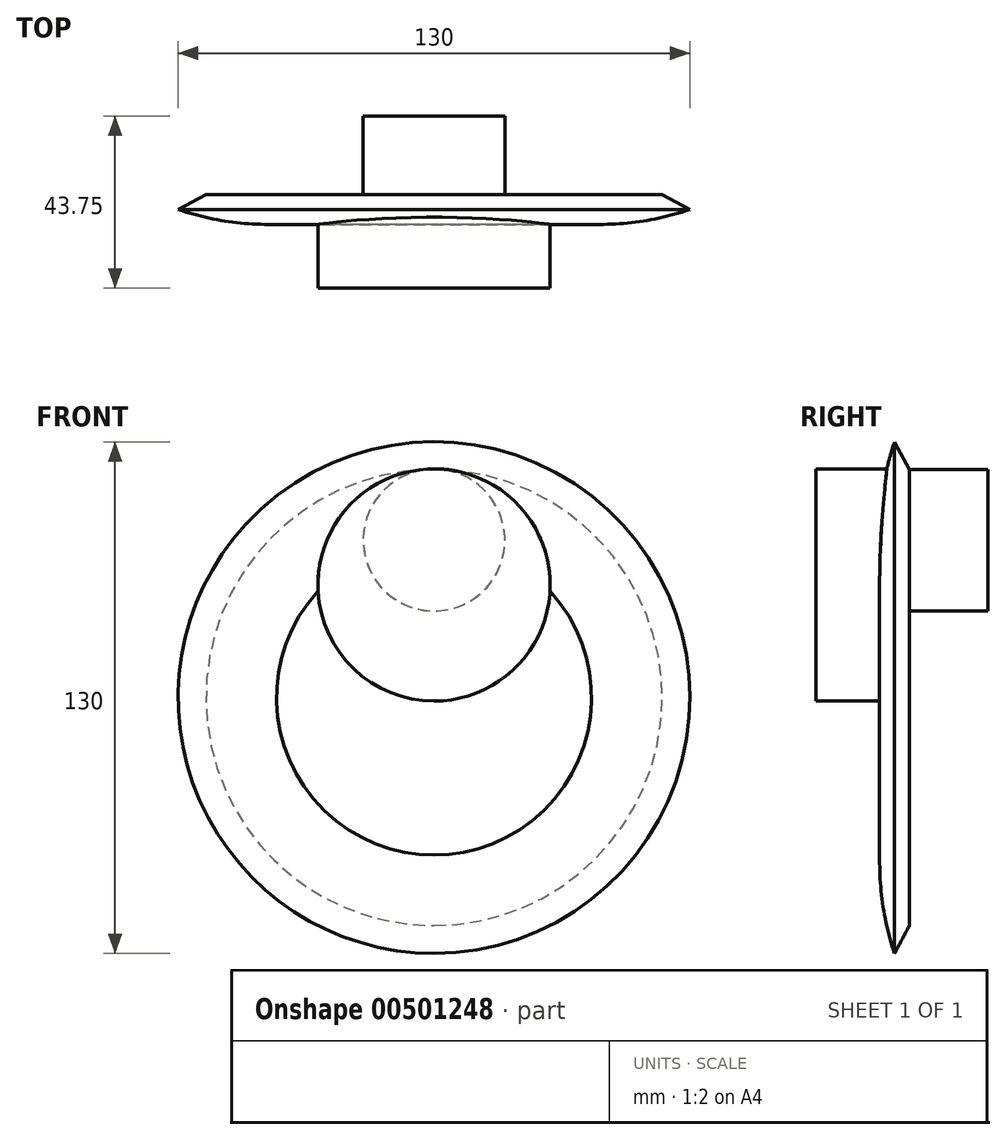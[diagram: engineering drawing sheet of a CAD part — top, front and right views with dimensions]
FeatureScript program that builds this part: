
annotation { "Feature Type Name" : "Feature", "Feature Type Description" : "" }
export const myFeature = defineFeature(function(context is Context, id is Id, definition is map)
    precondition{}
    {
        {
            var Q0;
            Q0=qCreatedBy(makeId("Right.planeOp"),FACE);
            var sketch = newSketch(context, id + "F0", { "sketchPlane" : qUnion([Q0])});
            skLineSegment(sketch, "E0", {"start": v(-3.75, -28.62) * mm, "end": v(3.75, -28.62) * mm});
            skLineSegment(sketch, "E1", {"start": v(-3.75, -28.62) * mm, "end": v(-3.75, 11.38) * mm});
            skFitSpline(sketch, "E2", {"points": [v(-3.75, 11.38) * mm, v(0, 36.38) * mm], "startDerivative": vector(-0.77, 26.48) * mm, "endDerivative": vector(7.66, 22.34) * mm});
            skLineSegment(sketch, "E3", {"start": v(3.75, -28.62) * mm, "end": v(3.75, 29.31) * mm});
            skLineSegment(sketch, "E4", {"start": v(0, 36.38) * mm, "end": v(3.75, 29.31) * mm});
            skSolve(sketch);
        }
        {
            var Q0;
            Q0=qCreatedBy(makeId("Front.planeOp"),FACE);
            var sketch = newSketch(context, id + "F1", { "sketchPlane" : qUnion([Q0])});
            skCircle(sketch, "E5", {"center": v(0, 0) * mm, "radius": 29.5 * mm});
            skSolve(sketch);
        }
        {
            var Q0;
            Q0=makeQuery(id+"F1.imprint","IMPRINT",FACE,{"disambiguationData":[TD([[makeQuery(id+"F1.imprint","IMPRINT",EDGE,{"derivedFrom":sQuery(id+"F1.wireOp",EDGE,"E5")}),1.0]])]});
            extrude(context, id + "F2", {"entities" : qUnion([Q0]), "depth" : 20 * mm});
        }
        {
            var Q0;
            Q0=makeQuery(id+"F0.imprint","IMPRINT",FACE,{"disambiguationData":[TD([[makeQuery(id+"F0.imprint","IMPRINT",EDGE,{"derivedFrom":sQuery(id+"F0.wireOp",EDGE,"E0")}),1.0]])]});
            var Q1;
            Q1=sQuery(id+"F0.wireOp",EDGE,"E0");
            revolve(context, id + "F3", {"operationType" : NewBodyOperationType.ADD, "entities" : qUnion([Q0]), "axis" : qUnion([Q1]), "revolveType" : RevolveType.FULL});
        }
        {
            var Q0;
            Q0=makeQuery(id+"F3.opRevolve","SWEPT_FACE",FACE,{"disambiguationData":[OSD([sQuery(id+"F0.wireOp",EDGE,"E3")])]});
            var sketch = newSketch(context, id + "F4", { "sketchPlane" : qUnion([Q0])});
            skCircle(sketch, "E6", {"center": v(0, 11.38) * mm, "radius": 18 * mm});
            skSolve(sketch);
        }
        {
            var Q0;
            Q0 = qSketchRegion(id + "F4", true);
            extrude(context, id + "F5", {"entities" : qUnion([Q0]), "operationType" : NewBodyOperationType.ADD, "depth" : 20 * mm});
        }
    });
